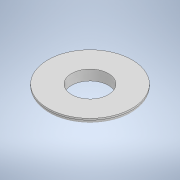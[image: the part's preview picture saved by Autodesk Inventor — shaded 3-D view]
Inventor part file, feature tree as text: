
AUTODESK INVENTOR PART (.ipt)
format: ipt  version: 2021 (Build 250183000, 183)  size: 126,464 bytes
history: native  units: mm
features: extrude x2, sketch x1, fillet x1
ambient origin geometry x8: Origin, YZ Plane, XZ Plane, XY Plane, X Axis, Y Axis, Z Axis, Center Point
bodies: Solid1 (feature_tree)
feature tree (4):
  sketch  "Sketch1"  dims[d0=45.5mm d1=104.0mm d2=55.5mm d3=7.0mm d4=0.0mm d5=5.75mm d6=0.0mm d7=5.0mm]
  extrude  "Extrusion1"  Depth=5.0mm
  extrude  "Extrusion2"  Depth=5.0mm
  fillet  "Fillet1"  Radius=7.0mm
